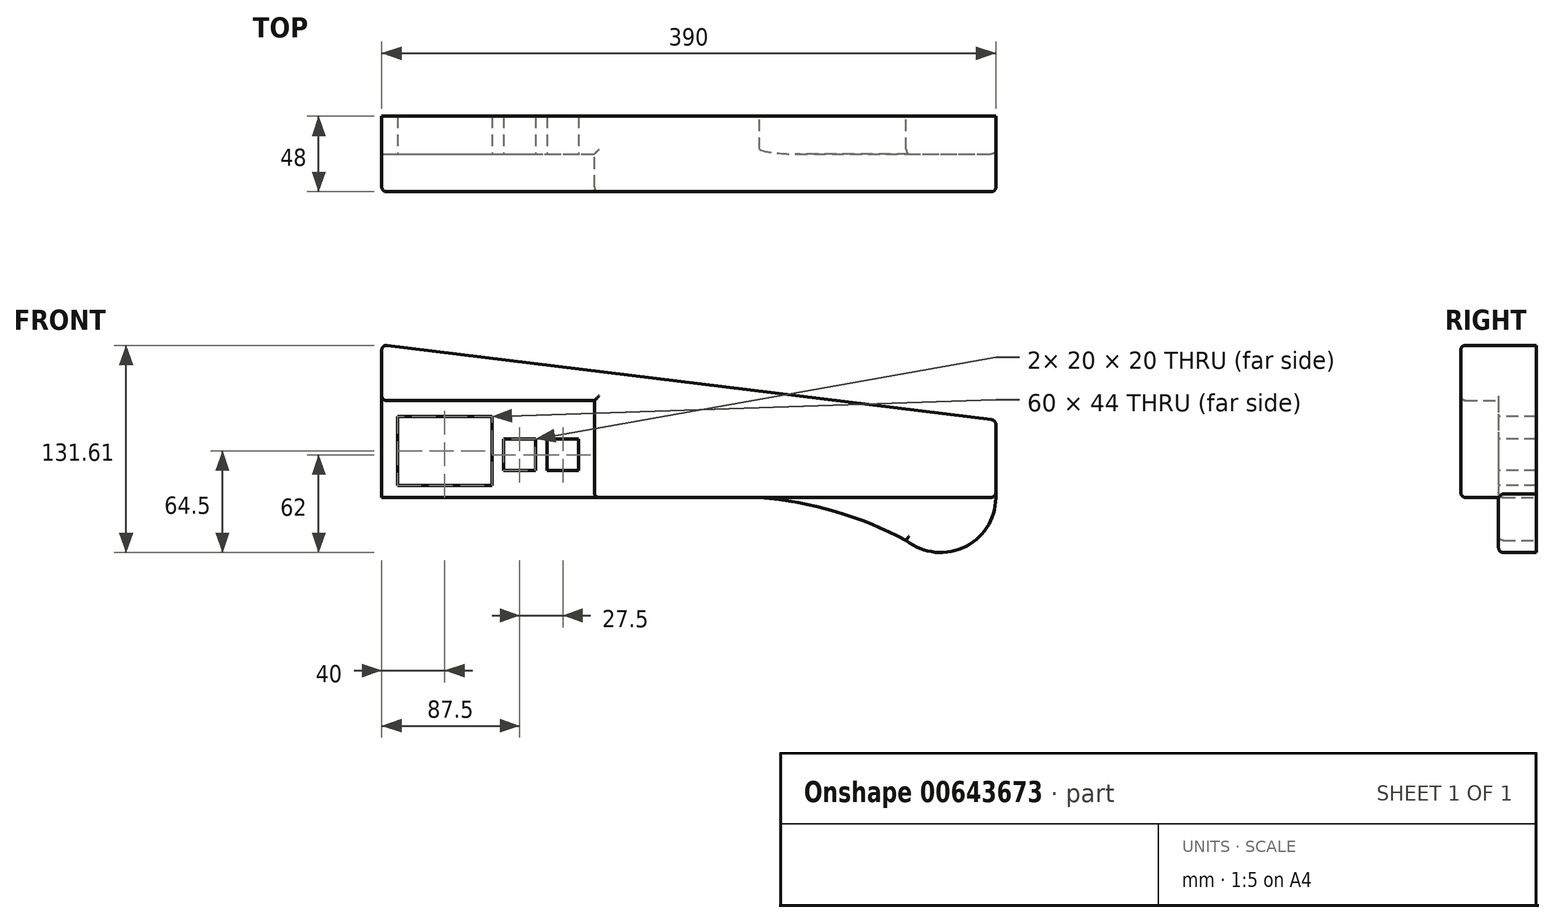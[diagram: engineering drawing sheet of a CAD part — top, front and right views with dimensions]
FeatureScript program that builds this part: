
annotation { "Feature Type Name" : "Feature", "Feature Type Description" : "" }
export const myFeature = defineFeature(function(context is Context, id is Id, definition is map)
    precondition{}
    {
        {
            var Q0;
            Q0=qCreatedBy(makeId("Front.planeOp"),FACE);
            var sketch = newSketch(context, id + "F0", { "sketchPlane" : qUnion([Q0])});
            skLineSegment(sketch, "E0.top", {"start": v(-195, 0) * mm, "end": v(45, 0) * mm});
            skLineSegment(sketch, "E0.left", {"start": v(-195, 97) * mm, "end": v(-195, 0) * mm});
            skLineSegment(sketch, "E0.right", {"start": v(195, 49) * mm, "end": v(195, 0) * mm});
            skLineSegment(sketch, "E1", {"start": v(-195, 97) * mm, "end": v(195, 49) * mm});
            skArc(sketch, "E2", {"start": v(138.06, -27.27) * mm, "mid": v(175.12, -31.57) * mm, "end": v(195, 0) * mm});
            skArc(sketch, "E3", {"start": v(138.06, -27.27) * mm, "mid": v(92.9, -8.98) * mm, "end": v(45, 0) * mm});
            skSolve(sketch);
        }
        {
            var Q0;
            Q0 = qSketchRegion(id + "F0", true);
            extrude(context, id + "F1", {"entities" : qUnion([Q0]), "depth" : 24 * mm, "offsetDistance" : 25 * mm});
        }
        {
            var Q0;
            Q0=makeQuery(id+"F1.opExtrude","CAP_FACE",FACE,{"disambiguationData":[OSD([sQuery(id+"F0.wireOp",EDGE,"E0.top"),sQuery(id+"F0.wireOp",EDGE,"E0.left"),sQuery(id+"F0.wireOp",EDGE,"E0.right"),sQuery(id+"F0.wireOp",EDGE,"E1"),sQuery(id+"F0.wireOp",EDGE,"E2"),sQuery(id+"F0.wireOp",EDGE,"E3")])],"isStart":false});
            var sketch = newSketch(context, id + "F2", { "sketchPlane" : qUnion([Q0])});
            skLineSegment(sketch, "E4.bottom", {"start": v(-60, 0) * mm, "end": v(195, 0) * mm});
            skLineSegment(sketch, "E4.left", {"start": v(-195, 61.5) * mm, "end": v(-195, 97) * mm});
            skLineSegment(sketch, "E4.right", {"start": v(195, 0) * mm, "end": v(195, 49) * mm});
            skLineSegment(sketch, "E5", {"start": v(-195, 97) * mm, "end": v(195, 49) * mm});
            skLineSegment(sketch, "E6", {"start": v(-195, 61.5) * mm, "end": v(-60, 61.5) * mm});
            skLineSegment(sketch, "E7", {"start": v(-60, 61.5) * mm, "end": v(-60, 0) * mm});
            skSolve(sketch);
        }
        {
            var Q0;
            Q0 = qSketchRegion(id + "F2", true);
            extrude(context, id + "F3", {"entities" : qUnion([Q0]), "operationType" : NewBodyOperationType.ADD, "depth" : 24 * mm, "offsetDistance" : 25 * mm});
        }
        {
            var Q0;
            {var subQ0=sQuery(id+"F0.wireOp",EDGE,"E0.left");var subQ1=sQuery(id+"F0.wireOp",EDGE,"E0.top");Q0=makeQuery(id+"F3.boolean.opBoolean","SPLIT",FACE,{"disambiguationData":[TD([makeQuery(id+"F1.opExtrude","SWEPT_FACE",FACE,{"disambiguationData":[OSD([subQ0])]})])],"derivedFrom":makeQuery(id+"F1.opExtrude","CAP_FACE",FACE,{"disambiguationData":[OSD([subQ1,subQ0,sQuery(id+"F0.wireOp",EDGE,"E0.right"),sQuery(id+"F0.wireOp",EDGE,"E1"),sQuery(id+"F0.wireOp",EDGE,"E2"),sQuery(id+"F0.wireOp",EDGE,"E3")])],"isStart":false})});}
            var sketch = newSketch(context, id + "F4", { "sketchPlane" : qUnion([Q0])});
            skLineSegment(sketch, "E8.bottom", {"start": v(-185, 51.5) * mm, "end": v(-125, 51.5) * mm});
            skLineSegment(sketch, "E8.top", {"start": v(-185, 7.5) * mm, "end": v(-125, 7.5) * mm});
            skLineSegment(sketch, "E8.left", {"start": v(-185, 51.5) * mm, "end": v(-185, 7.5) * mm});
            skLineSegment(sketch, "E8.right", {"start": v(-125, 51.5) * mm, "end": v(-125, 7.5) * mm});
            skLineSegment(sketch, "E9.bottom", {"start": v(-117.5, 37) * mm, "end": v(-97.5, 37) * mm});
            skLineSegment(sketch, "E9.top", {"start": v(-117.5, 17) * mm, "end": v(-97.5, 17) * mm});
            skLineSegment(sketch, "E9.left", {"start": v(-117.5, 37) * mm, "end": v(-117.5, 17) * mm});
            skLineSegment(sketch, "E9.right", {"start": v(-97.5, 37) * mm, "end": v(-97.5, 17) * mm});
            skLineSegment(sketch, "E10.bottom", {"start": v(-90, 37) * mm, "end": v(-70, 37) * mm});
            skLineSegment(sketch, "E10.top", {"start": v(-90, 17) * mm, "end": v(-70, 17) * mm});
            skLineSegment(sketch, "E10.left", {"start": v(-90, 37) * mm, "end": v(-90, 17) * mm});
            skLineSegment(sketch, "E10.right", {"start": v(-70, 37) * mm, "end": v(-70, 17) * mm});
            skSolve(sketch);
        }
        {
            var Q0;
            Q0 = qSketchRegion(id + "F4", true);
            extrude(context, id + "F5", {"entities" : qUnion([Q0]), "operationType" : NewBodyOperationType.REMOVE, "oppositeDirection" : true, "depth" : 24 * mm, "offsetDistance" : 25 * mm});
        }
        {
            var Q0;
            Q0=makeQuery(id+"F3.boolean.opBoolean","MERGE",EDGE,{"derivedFrom":[makeQuery(id+"F1.opExtrude","SWEPT_EDGE",EDGE,{"disambiguationData":[OSD([sQuery(id+"F0.wireOp",EDGE,"E0.right"),sQuery(id+"F0.wireOp",EDGE,"E1")])]}),makeQuery(id+"F3.opExtrude","SWEPT_EDGE",EDGE,{"disambiguationData":[OSD([sQuery(id+"F2.wireOp",EDGE,"E4.right"),sQuery(id+"F2.wireOp",EDGE,"E5")])]})]});
            var Q1;
            Q1=makeQuery(id+"F3.opExtrude","CAP_EDGE",EDGE,{"disambiguationData":[OSD([sQuery(id+"F2.wireOp",EDGE,"E4.left")])],"isStart":false});
            var Q2;
            Q2=makeQuery(id+"F3.opExtrude","CAP_EDGE",EDGE,{"disambiguationData":[OSD([sQuery(id+"F2.wireOp",EDGE,"E4.right")])],"isStart":false});
            var Q3;
            Q3=makeQuery(id+"F3.opExtrude","SWEPT_EDGE",EDGE,{"disambiguationData":[OSD([sQuery(id+"F0.wireOp",EDGE,"E0.left"),sQuery(id+"F2.wireOp",EDGE,"E4.left"),sQuery(id+"F2.wireOp",EDGE,"E6")])]});
            var Q4;
            Q4=makeQuery(id+"F3.opExtrude","CAP_EDGE",EDGE,{"disambiguationData":[OSD([sQuery(id+"F2.wireOp",EDGE,"E5")])],"isStart":false});
            var Q5;
            Q5=makeQuery(id+"F3.opExtrude","CAP_EDGE",EDGE,{"disambiguationData":[OSD([sQuery(id+"F2.wireOp",EDGE,"E6")])],"isStart":false});
            var Q6;
            Q6=makeQuery(id+"F3.opExtrude","CAP_EDGE",EDGE,{"disambiguationData":[OSD([sQuery(id+"F2.wireOp",EDGE,"E7")])],"isStart":false});
            var Q7;
            Q7=makeQuery(id+"F1.opExtrude","CAP_EDGE",EDGE,{"disambiguationData":[OSD([sQuery(id+"F0.wireOp",EDGE,"E2")])],"isStart":false});
            var Q8;
            Q8=makeQuery(id+"F1.opExtrude","CAP_EDGE",EDGE,{"disambiguationData":[OSD([sQuery(id+"F0.wireOp",EDGE,"E3")])],"isStart":false});
            var Q9;
            Q9=makeQuery(id+"F3.opExtrude","CAP_EDGE",EDGE,{"disambiguationData":[OSD([sQuery(id+"F2.wireOp",EDGE,"E4.bottom")])],"isStart":false});
            var Q10;
            Q10=makeQuery(id+"F3.boolean.opBoolean","MERGE",EDGE,{"derivedFrom":[makeQuery(id+"F1.opExtrude","SWEPT_EDGE",EDGE,{"disambiguationData":[OSD([sQuery(id+"F0.wireOp",EDGE,"E0.left"),sQuery(id+"F0.wireOp",EDGE,"E1")])]}),makeQuery(id+"F3.opExtrude","SWEPT_EDGE",EDGE,{"disambiguationData":[OSD([sQuery(id+"F2.wireOp",EDGE,"E4.left"),sQuery(id+"F2.wireOp",EDGE,"E5")])]})]});
            fillet(context, id + "F6", {"entities" : qUnion([Q0, Q1, Q2, Q3, Q4, Q5, Q6, Q7, Q8, Q9, Q10]), "radius" : 3 * mm, "tangentPropagation" : true, "allowEdgeOverflow" : false});
        }
        {
            var Q0;
            Q0=makeQuery(id+"F3.opExtrude","SWEPT_EDGE",EDGE,{"disambiguationData":[OSD([sQuery(id+"F0.wireOp",EDGE,"E2"),sQuery(id+"F2.wireOp",EDGE,"E4.bottom"),sQuery(id+"F2.wireOp",EDGE,"E4.right")])]});
            fillet(context, id + "F7", {"entities" : qUnion([Q0]), "radius" : 3 * mm, "tangentPropagation" : true, "allowEdgeOverflow" : false});
        }
        {
            var Q0;
            Q0=makeQuery(id+"F3.opExtrude","SWEPT_EDGE",EDGE,{"disambiguationData":[OSD([sQuery(id+"F0.wireOp",EDGE,"E0.top"),sQuery(id+"F2.wireOp",EDGE,"E4.bottom"),sQuery(id+"F2.wireOp",EDGE,"E7")])]});
            var Q1;
            Q1=makeQuery(id+"F1.opExtrude","CAP_EDGE",EDGE,{"disambiguationData":[OSD([sQuery(id+"F0.wireOp",EDGE,"E0.top")])],"isStart":false});
            fillet(context, id + "F8", {"entities" : qUnion([Q0, Q1]), "radius" : 3 * mm, "tangentPropagation" : true, "allowEdgeOverflow" : false});
        }
    });
